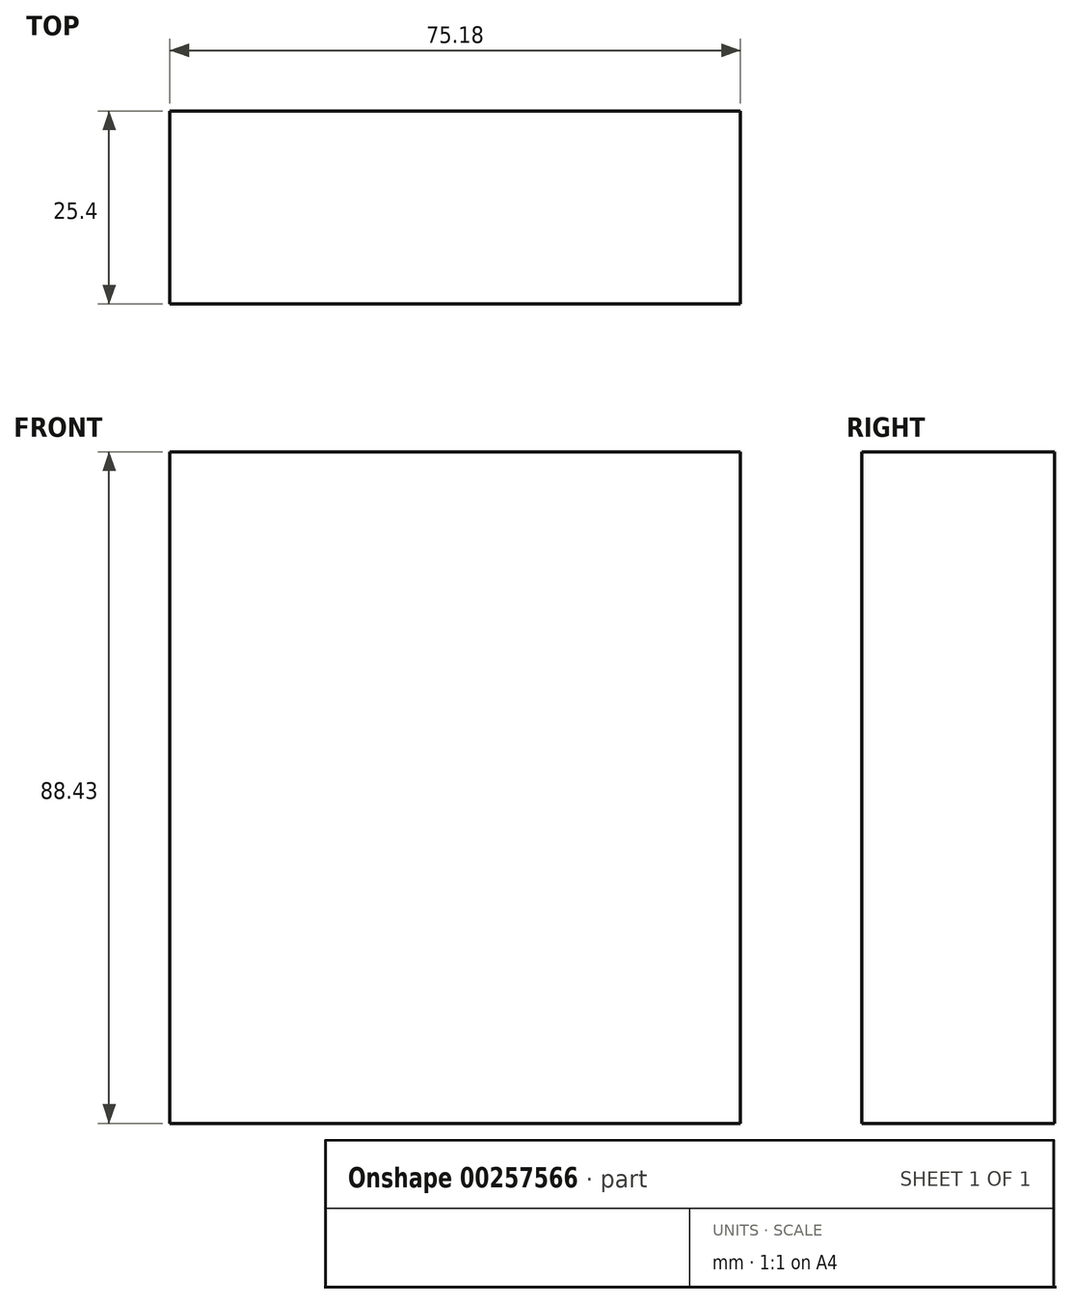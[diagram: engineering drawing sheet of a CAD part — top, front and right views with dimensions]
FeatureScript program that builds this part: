
annotation { "Feature Type Name" : "Feature", "Feature Type Description" : "" }
export const myFeature = defineFeature(function(context is Context, id is Id, definition is map)
    precondition{}
    {
        {
            var Q0;
            Q0=qCreatedBy(makeId("Front.planeOp"),FACE);
            var sketch = newSketch(context, id + "F0", { "sketchPlane" : qUnion([Q0])});
            skLineSegment(sketch, "E0.bottom", {"start": v(-14.84, 7.26) * mm, "end": v(-90.02, 7.26) * mm});
            skLineSegment(sketch, "E0.top", {"start": v(-14.84, 95.7) * mm, "end": v(-90.02, 95.7) * mm});
            skLineSegment(sketch, "E0.left", {"start": v(-14.84, 7.26) * mm, "end": v(-14.84, 95.7) * mm});
            skLineSegment(sketch, "E0.right", {"start": v(-90.02, 7.26) * mm, "end": v(-90.02, 95.7) * mm});
            skPoint(sketch, "E0.middle", {"position": v(-52.43, 51.47) * mm});
            skSolve(sketch);
        }
        {
            var Q0;
            Q0 = qSketchRegion(id + "F0", true);
            extrude(context, id + "F1", {"entities" : qUnion([Q0]), "depth" : 25.4 * mm});
        }
    });
